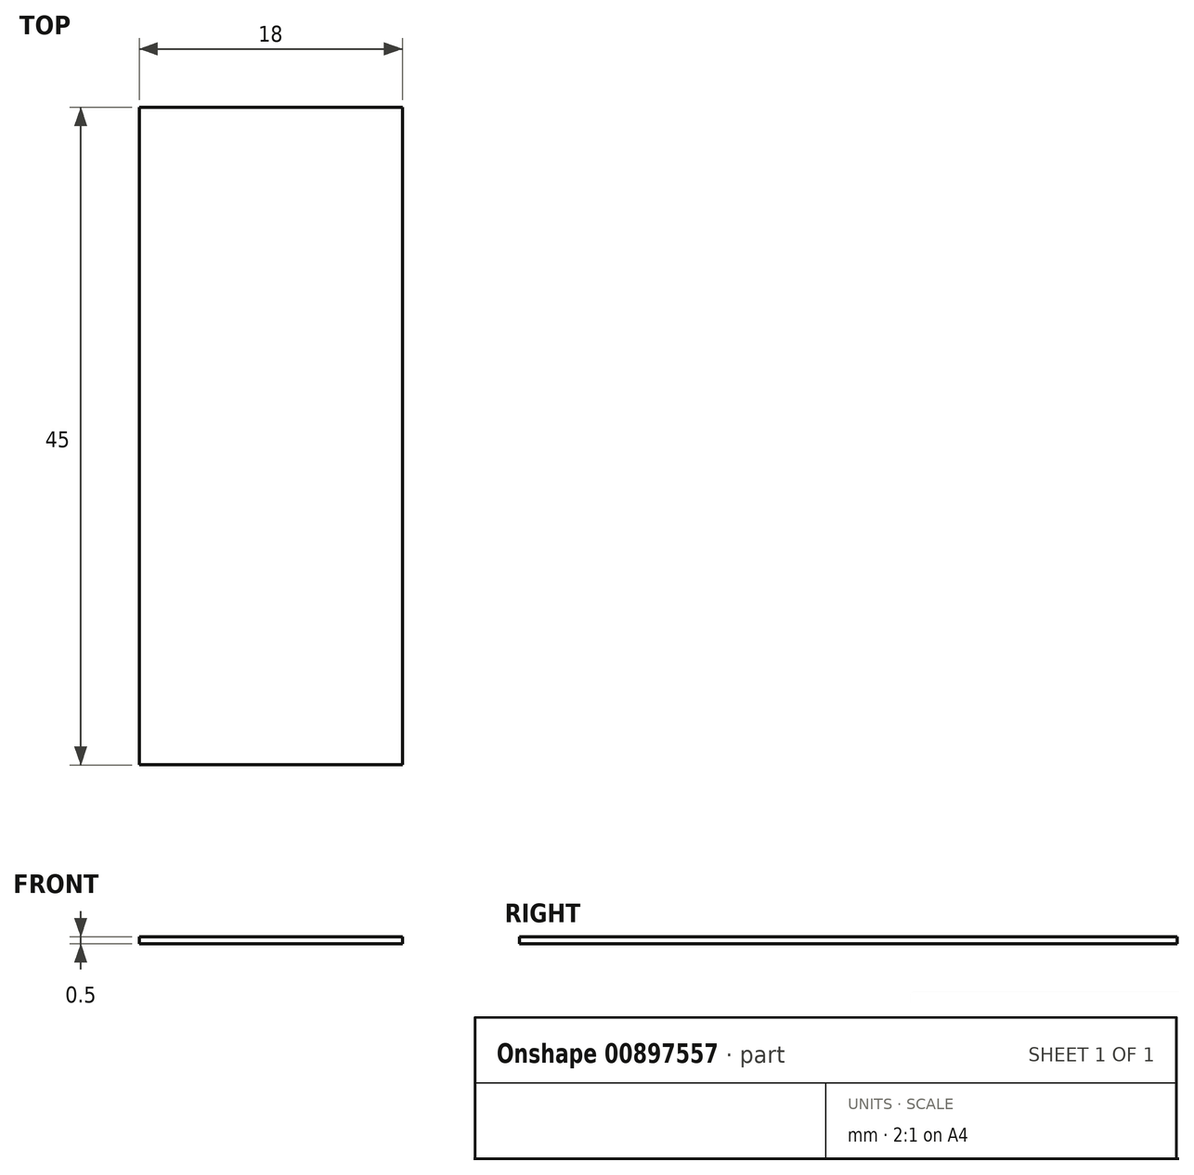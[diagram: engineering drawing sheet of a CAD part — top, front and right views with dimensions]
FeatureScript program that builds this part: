
annotation { "Feature Type Name" : "Feature", "Feature Type Description" : "" }
export const myFeature = defineFeature(function(context is Context, id is Id, definition is map)
    precondition{}
    {
        {
            var Q0;
            Q0=qCreatedBy(makeId("Top.planeOp"),FACE);
            var sketch = newSketch(context, id + "F0", { "sketchPlane" : qUnion([Q0])});
            skLineSegment(sketch, "E0.bottom", {"start": v(-15.03, 7.8) * mm, "end": v(2.97, 7.8) * mm});
            skLineSegment(sketch, "E0.top", {"start": v(-15.03, -37.2) * mm, "end": v(2.97, -37.2) * mm});
            skLineSegment(sketch, "E0.left", {"start": v(-15.03, 7.8) * mm, "end": v(-15.03, -37.2) * mm});
            skLineSegment(sketch, "E0.right", {"start": v(2.97, 7.8) * mm, "end": v(2.97, -37.2) * mm});
            skSolve(sketch);
        }
        {
            var Q0;
            Q0=qSketchRegion(id+"F0",true);
            extrude(context, id + "F1", {"entities" : qUnion([Q0]), "depth" : 0.5 * mm, "offsetDistance" : 25 * mm});
        }
    });
